# Revit family: 2200_Series_Aluminum_Mailboxes_Standard_Units
name_source: partatom
category: Specialty Equipment
revit_build: Autodesk Revit 2016 (Build: 20150714_1515(x64)
units: mm (PartAtom-declared; Revit-internal decimal feet)

## family parameters
Always vertical = Yes
Cut with Voids When Loaded = No
OmniClass Number = 23.40.90.14.11
OmniClass Title = Mail Boxes
Part Type = Normal
Room Calculation Point = No
Round Connector Dimension = Use Diameter
Shared = No
Work Plane-Based = No

## types (7) — shared parameters
Assembly Code = C1030910
Back Enclosure Material = Steel - Salsbury Finish - Clear
Depth = 15.5 "
Front Panel Material = Aluminum - Salsbury Finish - Aluminum
Height = 30 "
Lock Material = Stainless Steel -Salsbury Finish - Polished
Manufacturer = Salsbury Industries
MasterFormat Number = 10 55 00
MasterFormat Title = Postal Specialties
Trim Material = Aluminum - Salsbury Finish - Black
Type Comments = Aluminum Mailbox
Width = 23.25 "

## per-type parameters (varying)
- 2230: Description=Standard System - 30 #1 Doors; Divider 3=Yes; Divider 6 and 7 Offset=29.406 "; Dividers 1, 2, 4, 5=Yes; Dividers 6, 7=No; Door Location D1=Rack Ladder #1 Door : #1 Door; Door Location D10=Rack Ladder #1 Door : #1 Door; Door Location D11=Rack Ladder #1 Door : #1 Door; Door Location D12=Rack Ladder #1 Door : #1 Door; Door Location D13=Rack Ladder #1 Door : #1 Door; Door Location D14=Rack Ladder #1 Door : #1 Door; Door Location D15=Rack Ladder #1 Door : #1 Door; Door Location D16=Rack Ladder #1 Door : #1 Door; Door Location D17=Rack Ladder #1 Door : #1 Door; Door Location D18=Rack Ladder #1 Door : #1 Door; Door Location D19=Rack Ladder #1 Door : #1 Door; Door Location D2=Rack Ladder #1 Door : #1 Door; Door Location D20=Rack Ladder #1 Door : #1 Door; Door Location D21=Rack Ladder #1 Door : #1 Door; Door Location D22=Rack Ladder #1 Door : #1 Door; Door Location D23=Rack Ladder #1 Door : #1 Door; Door Location D24=Rack Ladder #1 Door : #1 Door; Door Location D25=Rack Ladder #1 Door : #1 Door; Door Location D26=Rack Ladder #1 Door : #1 Door; Door Location D27=Rack Ladder #1 Door : #1 Door; Door Location D28=Rack Ladder #1 Door : #1 Door; Door Location D29=Rack Ladder #1 Door : #1 Door; Door Location D3=Rack Ladder #1 Door : #1 Door; Door Location D30=Rack Ladder #1 Door : #1 Door; Door Location D31=Rack Ladder None : No Door; Door Location D32=Rack Ladder None : No Door; Door Location D33=Rack Ladder None : No Door; Door Location D34=Rack Ladder None : No Door; Door Location D35=Rack Ladder None : No Door; Door Location D36=Rack Ladder None : No Door; Door Location D37=Rack Ladder None : No Door; Door Location D38=Rack Ladder None : No Door; Door Location D39=Rack Ladder None : No Door; Door Location D4=Rack Ladder #1 Door : #1 Door; Door Location D40=Rack Ladder None : No Door; Door Location D5=Rack Ladder #1 Door : #1 Door; Door Location D6=Rack Ladder #1 Door : #1 Door; Door Location D7=Rack Ladder #1 Door : #1 Door; Door Location D8=Rack Ladder #1 Door : #1 Door; Door Location D9=Rack Ladder #1 Door : #1 Door; Horizontal Divider 2=Yes; Horizontal Divider 4=Yes; Horizontal Dividers 1 and 3=Yes; Model=2230; OmniClass 23 Number=23.40.90.14.11; OmniClass 23 Title=Mail Boxes; Rear Overhang=Yes; URL=www.mailboxes.com; Version=2.0 (06/30/18); Visible=Yes; Void 2 Offset=17.937 "; Void 4 Offset=6.063 "
- None: Description=Standard System - 30 #1 Doors; Divider 3=No; Divider 6 and 7 Offset=29.406 "; Dividers 1, 2, 4, 5=No; Dividers 6, 7=No; Door Location D1=Rack Ladder #1 Door : #1 Door; Door Location D10=Rack Ladder #1 Door : #1 Door; Door Location D11=Rack Ladder #1 Door : #1 Door; Door Location D12=Rack Ladder #1 Door : #1 Door; Door Location D13=Rack Ladder #1 Door : #1 Door; Door Location D14=Rack Ladder #1 Door : #1 Door; Door Location D15=Rack Ladder #1 Door : #1 Door; Door Location D16=Rack Ladder #1 Door : #1 Door; Door Location D17=Rack Ladder #1 Door : #1 Door; Door Location D18=Rack Ladder #1 Door : #1 Door; Door Location D19=Rack Ladder #1 Door : #1 Door; Door Location D2=Rack Ladder #1 Door : #1 Door; Door Location D20=Rack Ladder #1 Door : #1 Door; Door Location D21=Rack Ladder #1 Door : #1 Door; Door Location D22=Rack Ladder #1 Door : #1 Door; Door Location D23=Rack Ladder #1 Door : #1 Door; Door Location D24=Rack Ladder #1 Door : #1 Door; Door Location D25=Rack Ladder #1 Door : #1 Door; Door Location D26=Rack Ladder #1 Door : #1 Door; Door Location D27=Rack Ladder #1 Door : #1 Door; Door Location D28=Rack Ladder #1 Door : #1 Door; Door Location D29=Rack Ladder #1 Door : #1 Door; Door Location D3=Rack Ladder #1 Door : #1 Door; Door Location D30=Rack Ladder #1 Door : #1 Door; Door Location D31=Rack Ladder #1 Door : #1 Door; Door Location D32=Rack Ladder #1 Door : #1 Door; Door Location D33=Rack Ladder #1 Door : #1 Door; Door Location D34=Rack Ladder #1 Door : #1 Door; Door Location D35=Rack Ladder #1 Door : #1 Door; Door Location D36=Rack Ladder #1 Door : #1 Door; Door Location D37=Rack Ladder #1 Door : #1 Door; Door Location D38=Rack Ladder #1 Door : #1 Door; Door Location D39=Rack Ladder #1 Door : #1 Door; Door Location D4=Rack Ladder #1 Door : #1 Door; Door Location D40=Rack Ladder #1 Door : #1 Door; Door Location D5=Rack Ladder #1 Door : #1 Door; Door Location D6=Rack Ladder #1 Door : #1 Door; Door Location D7=Rack Ladder #1 Door : #1 Door; Door Location D8=Rack Ladder #1 Door : #1 Door; Door Location D9=Rack Ladder #1 Door : #1 Door; Horizontal Divider 2=No; Horizontal Divider 4=No; Horizontal Dividers 1 and 3=No; Model=2230; Rear Overhang=No; Version=1.0 (04/30/17); Visible=No; Void 2 Offset=17.937 "; Void 4 Offset=6.063 "
- 2220: Description=Standard System - 20 #2 Doors; Divider 3=Yes; Divider 6 and 7 Offset=29.406 "; Dividers 1, 2, 4, 5=No; Dividers 6, 7=Yes; Door Location D1=Rack Ladder None : No Door; Door Location D10=Rack Ladder None : No Door; Door Location D11=Rack Ladder None : No Door; Door Location D12=Rack Ladder #2 Door : #2 Door; Door Location D13=Rack Ladder None : No Door; Door Location D14=Rack Ladder None : No Door; Door Location D15=Rack Ladder #2 Door : #2 Door; Door Location D16=Rack Ladder None : No Door; Door Location D17=Rack Ladder None : No Door; Door Location D18=Rack Ladder #2 Door : #2 Door; Door Location D19=Rack Ladder None : No Door; Door Location D2=Rack Ladder None : No Door; Door Location D20=Rack Ladder None : No Door; Door Location D21=Rack Ladder #2 Door : #2 Door; Door Location D22=Rack Ladder None : No Door; Door Location D23=Rack Ladder None : No Door; Door Location D24=Rack Ladder #2 Door : #2 Door; Door Location D25=Rack Ladder None : No Door; Door Location D26=Rack Ladder None : No Door; Door Location D27=Rack Ladder #2 Door : #2 Door; Door Location D28=Rack Ladder None : No Door; Door Location D29=Rack Ladder None : No Door; Door Location D3=Rack Ladder #2 Door : #2 Door; Door Location D30=Rack Ladder #2 Door : #2 Door; Door Location D31=Rack Ladder #2 Door : #2 Door; Door Location D32=Rack Ladder #2 Door : #2 Door; Door Location D33=Rack Ladder #2 Door : #2 Door; Door Location D34=Rack Ladder #2 Door : #2 Door; Door Location D35=Rack Ladder #2 Door : #2 Door; Door Location D36=Rack Ladder #2 Door : #2 Door; Door Location D37=Rack Ladder #2 Door : #2 Door; Door Location D38=Rack Ladder #2 Door : #2 Door; Door Location D39=Rack Ladder #2 Door : #2 Door; Door Location D4=Rack Ladder None : No Door; Door Location D40=Rack Ladder #2 Door : #2 Door; Door Location D5=Rack Ladder None : No Door; Door Location D6=Rack Ladder #2 Door : #2 Door; Door Location D7=Rack Ladder None : No Door; Door Location D8=Rack Ladder None : No Door; Door Location D9=Rack Ladder #2 Door : #2 Door; Horizontal Divider 2=Yes; Horizontal Divider 4=Yes; Horizontal Dividers 1 and 3=Yes; Model=2220; OmniClass 23 Number=23.40.90.14.11; OmniClass 23 Title=Mail Boxes; Rear Overhang=Yes; URL=www.mailboxes.com; Version=2.0 (06/30/18); Visible=Yes; Void 2 Offset=17.937 "; Void 4 Offset=6.063 "
- 2218: Description=Standard System - 16 #2 Doors; 2 #3 Doors; Divider 3=Yes; Divider 6 and 7 Offset=23.437 "; Dividers 1, 2, 4, 5=No; Dividers 6, 7=Yes; Door Location D1=Rack Ladder None : No Door; Door Location D10=Rack Ladder None : No Door; Door Location D11=Rack Ladder None : No Door; Door Location D12=Rack Ladder #2 Door : #2 Door; Door Location D13=Rack Ladder None : No Door; Door Location D14=Rack Ladder None : No Door; Door Location D15=Rack Ladder #2 Door : #2 Door; Door Location D16=Rack Ladder None : No Door; Door Location D17=Rack Ladder None : No Door; Door Location D18=Rack Ladder #2 Door : #2 Door; Door Location D19=Rack Ladder None : No Door; Door Location D2=Rack Ladder None : No Door; Door Location D20=Rack Ladder None : No Door; Door Location D21=Rack Ladder #2 Door : #2 Door; Door Location D22=Rack Ladder None : No Door; Door Location D23=Rack Ladder None : No Door; Door Location D24=Rack Ladder #2 Door : #2 Door; Door Location D25=Rack Ladder None : No Door; Door Location D26=Rack Ladder None : No Door; Door Location D27=Rack Ladder #3 Door : #3 Door; Door Location D28=Rack Ladder None : No Door; Door Location D29=Rack Ladder None : No Door; Door Location D3=Rack Ladder #2 Door : #2 Door; Door Location D30=Rack Ladder #3 Door : #3 Door; Door Location D31=Rack Ladder #2 Door : #2 Door; Door Location D32=Rack Ladder #2 Door : #2 Door; Door Location D33=Rack Ladder #2 Door : #2 Door; Door Location D34=Rack Ladder #2 Door : #2 Door; Door Location D35=Rack Ladder #2 Door : #2 Door; Door Location D36=Rack Ladder #2 Door : #2 Door; Door Location D37=Rack Ladder #2 Door : #2 Door; Door Location D38=Rack Ladder #2 Door : #2 Door; Door Location D39=Rack Ladder None : No Door; Door Location D4=Rack Ladder None : No Door; Door Location D40=Rack Ladder None : No Door; Door Location D5=Rack Ladder None : No Door; Door Location D6=Rack Ladder #2 Door : #2 Door; Door Location D7=Rack Ladder None : No Door; Door Location D8=Rack Ladder None : No Door; Door Location D9=Rack Ladder #2 Door : #2 Door; Horizontal Divider 2=Yes; Horizontal Divider 4=Yes; Horizontal Dividers 1 and 3=Yes; Model=2218; OmniClass 23 Number=23.40.90.14.11; OmniClass 23 Title=Mail Boxes; Rear Overhang=Yes; URL=www.mailboxes.com; Version=2.0 (06/30/18); Visible=Yes; Void 2 Offset=17.937 "; Void 4 Offset=6.063 "
- 2214: Description=Standard System - 12 #2 Doors; 2 #4 Doors; Divider 3=Yes; Divider 6 and 7 Offset=17.5 "; Dividers 1, 2, 4, 5=No; Dividers 6, 7=Yes; Door Location D1=Rack Ladder None : No Door; Door Location D10=Rack Ladder None : No Door; Door Location D11=Rack Ladder None : No Door; Door Location D12=Rack Ladder #2 Door : #2 Door; Door Location D13=Rack Ladder None : No Door; Door Location D14=Rack Ladder None : No Door; Door Location D15=Rack Ladder #2 Door : #2 Door; Door Location D16=Rack Ladder None : No Door; Door Location D17=Rack Ladder None : No Door; Door Location D18=Rack Ladder #2 Door : #2 Door; Door Location D19=Rack Ladder None : No Door; Door Location D2=Rack Ladder None : No Door; Door Location D20=Rack Ladder None : No Door; Door Location D21=Rack Ladder None : No Door; Door Location D22=Rack Ladder None : No Door; Door Location D23=Rack Ladder None : No Door; Door Location D24=Rack Ladder None : No Door; Door Location D25=Rack Ladder None : No Door; Door Location D26=Rack Ladder None : No Door; Door Location D27=Rack Ladder #4 Door : #4 Door; Door Location D28=Rack Ladder None : No Door; Door Location D29=Rack Ladder None : No Door; Door Location D3=Rack Ladder #2 Door : #2 Door; Door Location D30=Rack Ladder #4 Door : #4 Door; Door Location D31=Rack Ladder #2 Door : #2 Door; Door Location D32=Rack Ladder #2 Door : #2 Door; Door Location D33=Rack Ladder #2 Door : #2 Door; Door Location D34=Rack Ladder #2 Door : #2 Door; Door Location D35=Rack Ladder #2 Door : #2 Door; Door Location D36=Rack Ladder #2 Door : #2 Door; Door Location D37=Rack Ladder None : No Door; Door Location D38=Rack Ladder None : No Door; Door Location D39=Rack Ladder None : No Door; Door Location D4=Rack Ladder None : No Door; Door Location D40=Rack Ladder None : No Door; Door Location D5=Rack Ladder None : No Door; Door Location D6=Rack Ladder #2 Door : #2 Door; Door Location D7=Rack Ladder None : No Door; Door Location D8=Rack Ladder None : No Door; Door Location D9=Rack Ladder #2 Door : #2 Door; Horizontal Divider 2=Yes; Horizontal Divider 4=No; Horizontal Dividers 1 and 3=Yes; Model=2214; OmniClass 23 Number=23.40.90.14.11; OmniClass 23 Title=Mail Boxes; Rear Overhang=Yes; URL=www.mailboxes.com; Version=2.0 (06/30/18); Visible=Yes; Void 2 Offset=17.937 "; Void 4 Offset=0 "
- 2210: Description=Standard System - 10 #3 Doors; Divider 3=Yes; Divider 6 and 7 Offset=29.406 "; Dividers 1, 2, 4, 5=No; Dividers 6, 7=No; Door Location D1=Rack Ladder None : No Door; Door Location D10=Rack Ladder None : No Door; Door Location D11=Rack Ladder None : No Door; Door Location D12=Rack Ladder #3 Door : #3 Door; Door Location D13=Rack Ladder None : No Door; Door Location D14=Rack Ladder None : No Door; Door Location D15=Rack Ladder #3 Door : #3 Door; Door Location D16=Rack Ladder None : No Door; Door Location D17=Rack Ladder None : No Door; Door Location D18=Rack Ladder #3 Door : #3 Door; Door Location D19=Rack Ladder None : No Door; Door Location D2=Rack Ladder None : No Door; Door Location D20=Rack Ladder None : No Door; Door Location D21=Rack Ladder #3 Door : #3 Door; Door Location D22=Rack Ladder None : No Door; Door Location D23=Rack Ladder None : No Door; Door Location D24=Rack Ladder #3 Door : #3 Door; Door Location D25=Rack Ladder None : No Door; Door Location D26=Rack Ladder None : No Door; Door Location D27=Rack Ladder #3 Door : #3 Door; Door Location D28=Rack Ladder None : No Door; Door Location D29=Rack Ladder None : No Door; Door Location D3=Rack Ladder #3 Door : #3 Door; Door Location D30=Rack Ladder #3 Door : #3 Door; Door Location D31=Rack Ladder None : No Door; Door Location D32=Rack Ladder None : No Door; Door Location D33=Rack Ladder None : No Door; Door Location D34=Rack Ladder None : No Door; Door Location D35=Rack Ladder None : No Door; Door Location D36=Rack Ladder None : No Door; Door Location D37=Rack Ladder None : No Door; Door Location D38=Rack Ladder None : No Door; Door Location D39=Rack Ladder None : No Door; Door Location D4=Rack Ladder None : No Door; Door Location D40=Rack Ladder None : No Door; Door Location D5=Rack Ladder None : No Door; Door Location D6=Rack Ladder #3 Door : #3 Door; Door Location D7=Rack Ladder None : No Door; Door Location D8=Rack Ladder None : No Door; Door Location D9=Rack Ladder #3 Door : #3 Door; Horizontal Divider 2=Yes; Horizontal Divider 4=Yes; Horizontal Dividers 1 and 3=Yes; Model=2210; OmniClass 23 Number=23.40.90.14.11; OmniClass 23 Title=Mail Boxes; Rear Overhang=Yes; URL=www.mailboxes.com; Version=2.0 (06/30/18); Visible=Yes; Void 2 Offset=17.937 "; Void 4 Offset=6.063 "
- 2206: Description=Standard System - 2 #3 Doors; 4 #4 Doors; Divider 3=Yes; Divider 6 and 7 Offset=29.406 "; Dividers 1, 2, 4, 5=No; Dividers 6, 7=No; Door Location D1=Rack Ladder None : No Door; Door Location D10=Rack Ladder None : No Door; Door Location D11=Rack Ladder None : No Door; Door Location D12=Rack Ladder None : No Door; Door Location D13=Rack Ladder None : No Door; Door Location D14=Rack Ladder None : No Door; Door Location D15=Rack Ladder #4 Door : #4 Door; Door Location D16=Rack Ladder None : No Door; Door Location D17=Rack Ladder None : No Door; Door Location D18=Rack Ladder #4 Door : #4 Door; Door Location D19=Rack Ladder None : No Door; Door Location D2=Rack Ladder None : No Door; Door Location D20=Rack Ladder None : No Door; Door Location D21=Rack Ladder None : No Door; Door Location D22=Rack Ladder None : No Door; Door Location D23=Rack Ladder None : No Door; Door Location D24=Rack Ladder None : No Door; Door Location D25=Rack Ladder None : No Door; Door Location D26=Rack Ladder None : No Door; Door Location D27=Rack Ladder #4 Door : #4 Door; Door Location D28=Rack Ladder None : No Door; Door Location D29=Rack Ladder None : No Door; Door Location D3=Rack Ladder #3 Door : #3 Door; Door Location D30=Rack Ladder #4 Door : #4 Door; Door Location D31=Rack Ladder None : No Door; Door Location D32=Rack Ladder None : No Door; Door Location D33=Rack Ladder None : No Door; Door Location D34=Rack Ladder None : No Door; Door Location D35=Rack Ladder None : No Door; Door Location D36=Rack Ladder None : No Door; Door Location D37=Rack Ladder None : No Door; Door Location D38=Rack Ladder None : No Door; Door Location D39=Rack Ladder None : No Door; Door Location D4=Rack Ladder None : No Door; Door Location D40=Rack Ladder None : No Door; Door Location D5=Rack Ladder None : No Door; Door Location D6=Rack Ladder #3 Door : #3 Door; Door Location D7=Rack Ladder None : No Door; Door Location D8=Rack Ladder None : No Door; Door Location D9=Rack Ladder None : No Door; Horizontal Divider 2=No; Horizontal Divider 4=No; Horizontal Dividers 1 and 3=Yes; Model=2206; OmniClass 23 Number=23.40.90.14.11; OmniClass 23 Title=Mail Boxes; Rear Overhang=Yes; URL=www.mailboxes.com; Version=2.0 (06/30/18); Visible=Yes; Void 2 Offset=0 "; Void 4 Offset=0 "

## geometry (parser evidence)
native form markers: Extrusion x2, Sweep x13
no freeform markers — native parametric forms only
